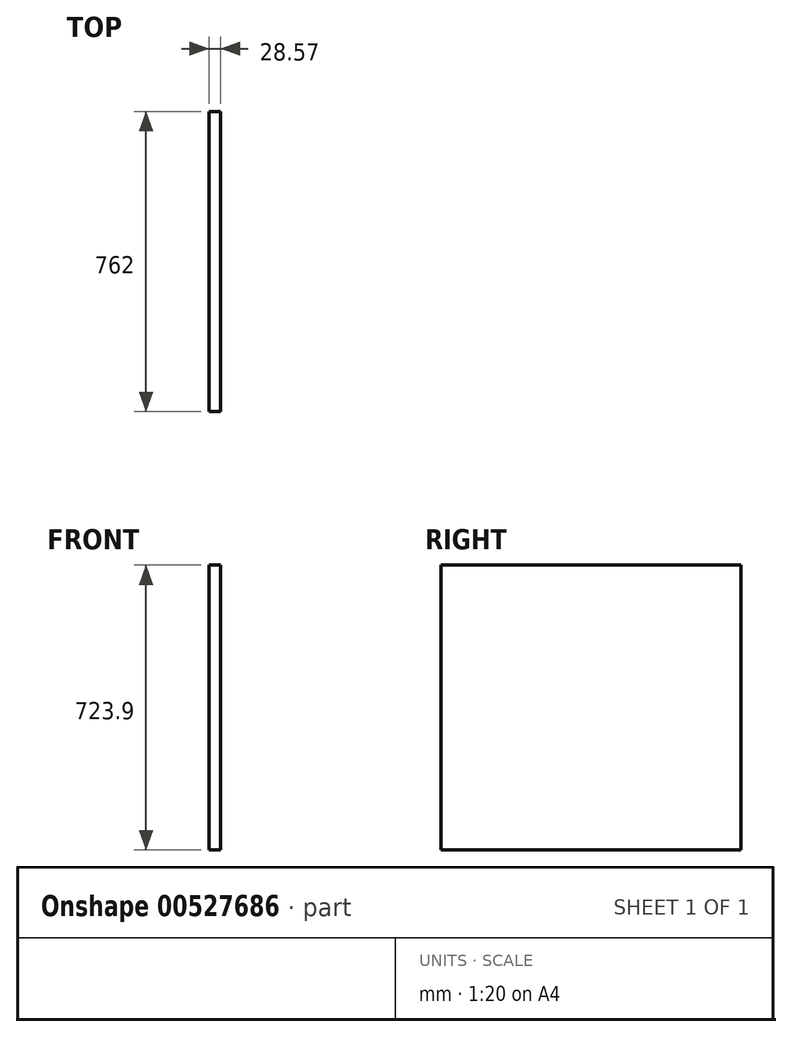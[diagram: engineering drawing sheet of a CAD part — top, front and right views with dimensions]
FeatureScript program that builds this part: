
annotation { "Feature Type Name" : "Feature", "Feature Type Description" : "" }
export const myFeature = defineFeature(function(context is Context, id is Id, definition is map)
    precondition{}
    {
        {
            var Q0;
            Q0=qCreatedBy(makeId("Right.planeOp"),FACE);
            var sketch = newSketch(context, id + "F0", { "sketchPlane" : qUnion([Q0])});
            skLineSegment(sketch, "E0.bottom", {"start": v(381, 361.95) * mm, "end": v(-381, 361.95) * mm});
            skLineSegment(sketch, "E0.top", {"start": v(381, -361.95) * mm, "end": v(-381, -361.95) * mm});
            skLineSegment(sketch, "E0.left", {"start": v(381, 361.95) * mm, "end": v(381, -361.95) * mm});
            skLineSegment(sketch, "E0.right", {"start": v(-381, 361.95) * mm, "end": v(-381, -361.95) * mm});
            skPoint(sketch, "E0.middle", {"position": v(0, 0) * mm});
            skSolve(sketch);
        }
        {
            var Q0;
            Q0=makeQuery(id+"F0.imprint","IMPRINT",FACE,{"disambiguationData":[TD([[makeQuery(id+"F0.imprint","IMPRINT",EDGE,{"derivedFrom":sQuery(id+"F0.wireOp",EDGE,"E0.bottom")}),1.0]])]});
            extrude(context, id + "F1", {"entities" : qUnion([Q0]), "depth" : 28.57 * mm, "offsetDistance" : 25.4 * mm});
        }
    });
